# Revit family: Runtal-RF-1
name_source: partatom
category: Mechanical Equipment
units: mm (PartAtom-declared; Revit-internal decimal feet)

## family parameters
Classification Number = 23.75.10.14.14
Cut with Voids When Loaded = No
Host = Face
Maintain Annotation Orientation = No
Part Type = Normal
Room Calculation Point = No
Round Connector Dimension = Use Diameter
Shared = No

## types (1)
- Radiator-RF_1-Runtal-Commercial
    Actual Length = 508 mm  [stored 1.66667 ft]
    Assembly Code = D3020
    Casing = Powder Coated-Runtal-W-White
    Default Elevation = 1219.2 mm  [stored 4 ft]
    Description = RF radiators are mounted horizontally and consist of two rows of fins sandwiched between two layers of panels.
    Fin Height = 67 mm
    Fin Length = 431.8 mm  [stored 1.41667 ft]
    Frame = UHMW, White
    Grille = Yes
    Grille Visibility = Yes
    Height = 144.78 mm
    Lamelle = Yes
    Length = 508 mm  [stored 1.66667 ft]
    Logo = Paint-Runtal-B-Black Matte
    Manufacturer = Runtal Radiators
    Model = RF-1
    URL = http://www.runtalnorthamerica.com

note: [stored X ft] marks values corroborated as IEEE doubles in the binary element streams (Revit-internal decimal feet)

## geometry (parser evidence)
native form markers: Blend x6, Sweep x13
no freeform markers — native parametric forms only
